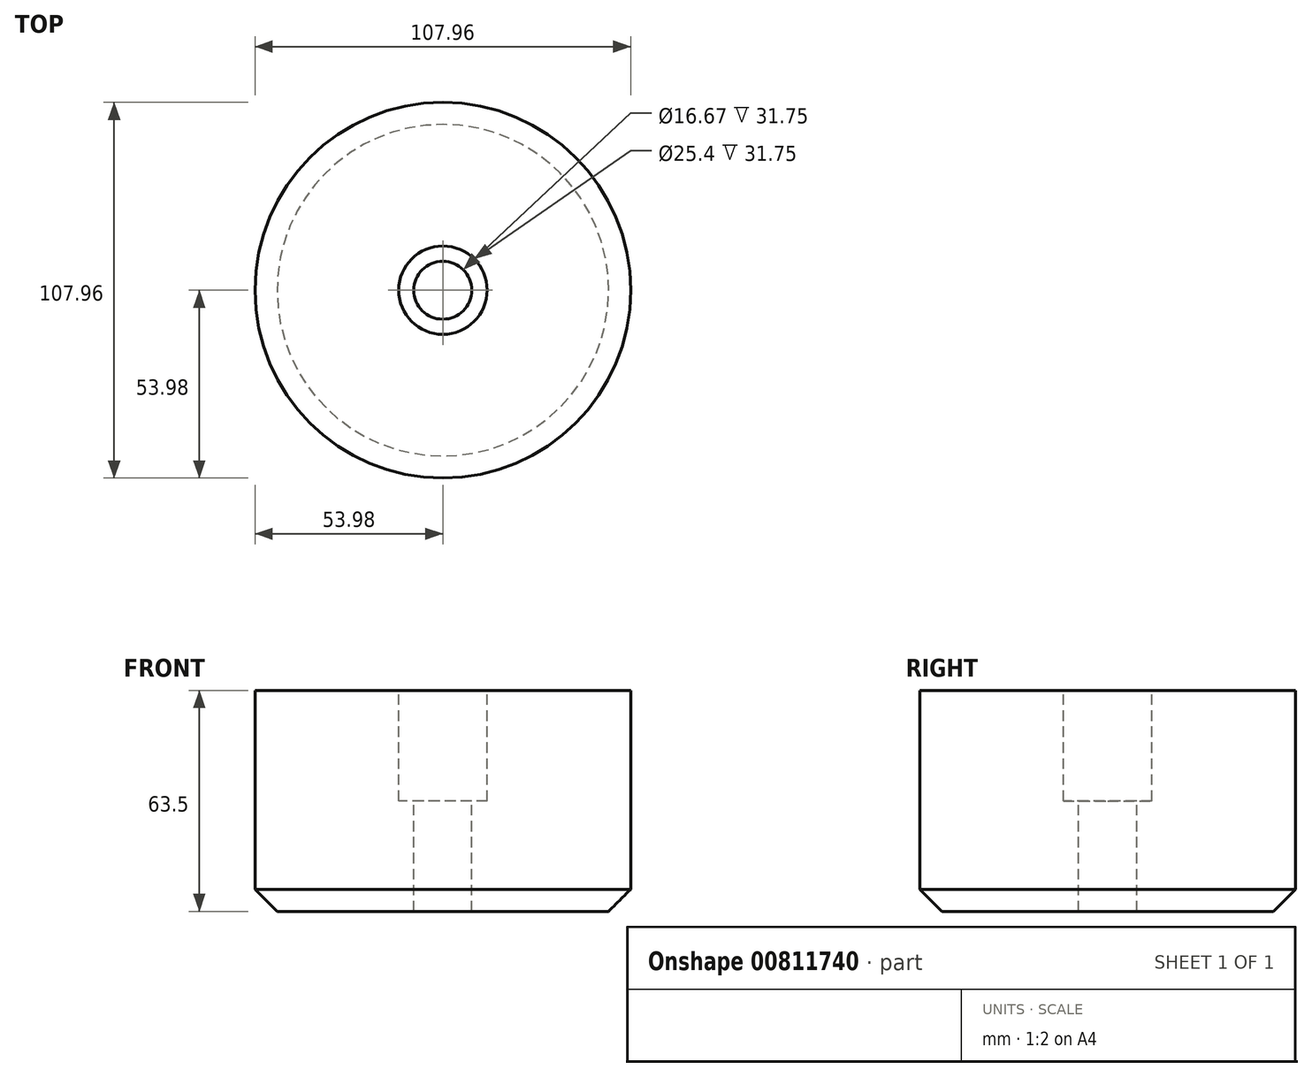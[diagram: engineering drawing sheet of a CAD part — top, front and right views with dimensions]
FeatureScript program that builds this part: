
annotation { "Feature Type Name" : "Feature", "Feature Type Description" : "" }
export const myFeature = defineFeature(function(context is Context, id is Id, definition is map)
    precondition{}
    {
        {
            var Q0;
            Q0=qCreatedBy(makeId("Top.planeOp"),FACE);
            var sketch = newSketch(context, id + "F0", { "sketchPlane" : qUnion([Q0])});
            skCircle(sketch, "E0", {"center": v(0, 0) * mm, "radius": 53.98 * mm});
            skSolve(sketch);
        }
        {
            var Q0;
            Q0 = qSketchRegion(id + "F0", true);
            extrude(context, id + "F1", {"entities" : qUnion([Q0]), "depth" : 63.5 * mm, "offsetDistance" : 25.4 * mm});
        }
        {
            var Q0;
            Q0=makeQuery(id+"F1.opExtrude","CAP_FACE",FACE,{"disambiguationData":[OSD([sQuery(id+"F0.wireOp",EDGE,"E0")])],"isStart":false});
            var sketch = newSketch(context, id + "F2", { "sketchPlane" : qUnion([Q0])});
            skPoint(sketch, "E1", {"position": v(0, 0) * mm});
            skSolve(sketch);
        }
        {
            var Q0;
            Q0=sQuery(id+"F2.wireOp",VERTEX,"E1");
            var Q1;
            Q1=makeQuery(id+"F1.opExtrude","SWEPT_BODY",BODY,{"disambiguationData":[OSD([sQuery(id+"F0.wireOp",EDGE,"E0")])]});
            hole(context, id + "F3", {"style" : HoleStyle.C_BORE, "endStyle" : HoleEndStyle.THROUGH, "holeDiameter" : 16.67 * mm, "cBoreDiameter" : 25.4 * mm, "cBoreDepth" : 31.75 * mm, "majorDiameter" : 15.88 * mm, "tappedDepth" : 48.27 * mm, "tapClearance" : 3, "startFromSketch" : true, "locations" : qUnion([Q0]), "scope" : qUnion([Q1])});
        }
        {
            var Q0;
            Q0=makeQuery(id+"F1.opExtrude","CAP_EDGE",EDGE,{"disambiguationData":[OSD([sQuery(id+"F0.wireOp",EDGE,"E0")])],"isStart":true});
            chamfer(context, id + "F4", {"entities" : qUnion([Q0]), "width" : 6.35 * mm, "tangentPropagation" : true});
        }
    });
